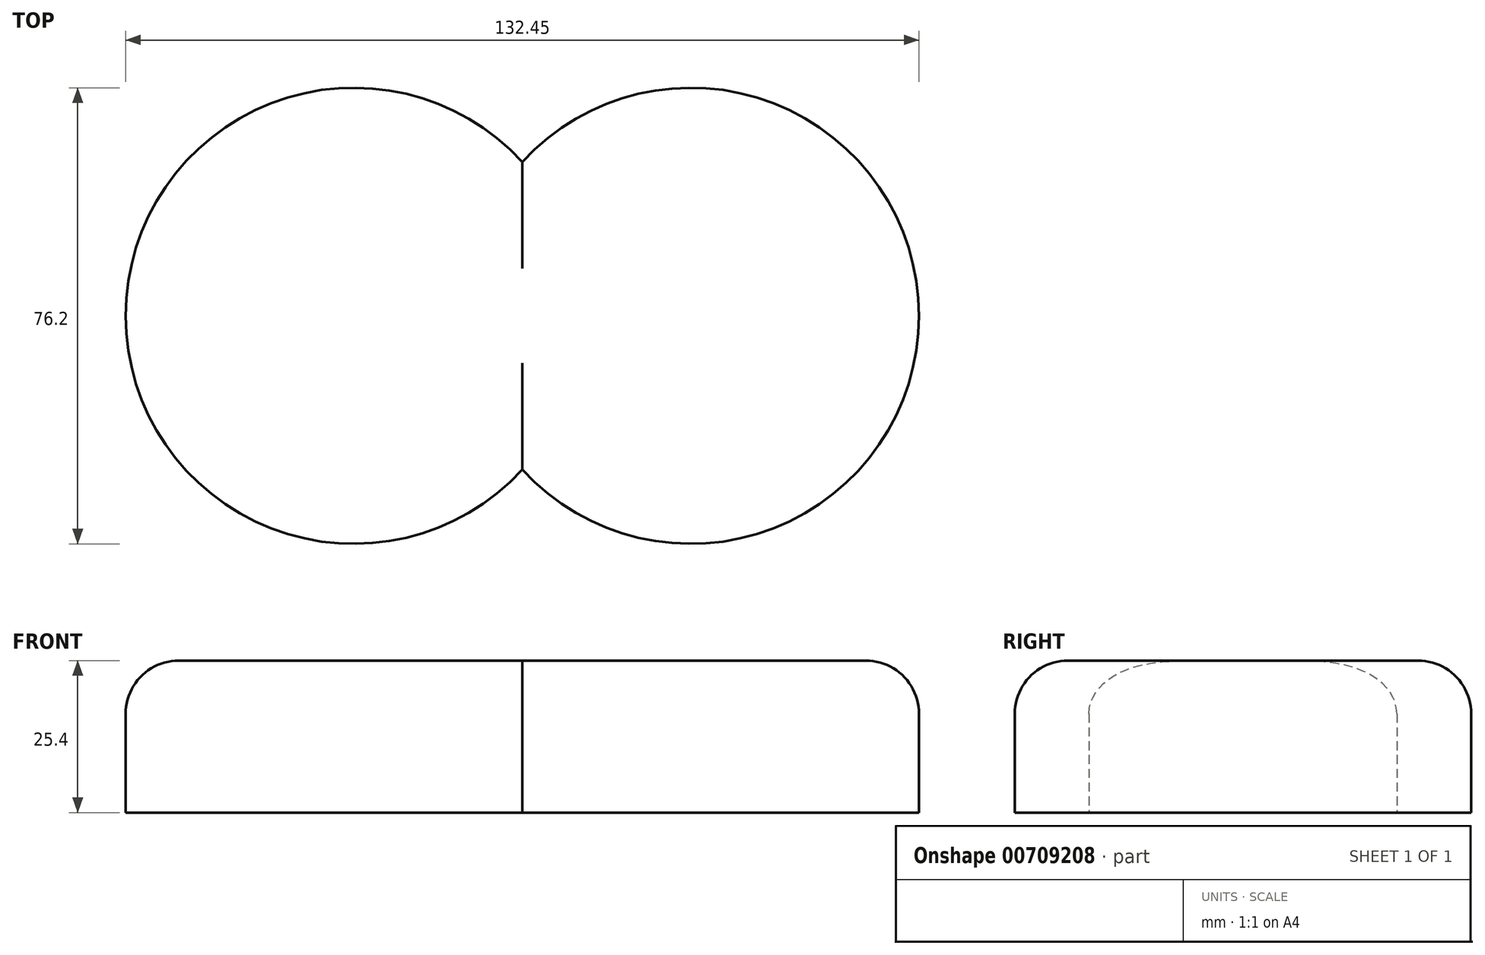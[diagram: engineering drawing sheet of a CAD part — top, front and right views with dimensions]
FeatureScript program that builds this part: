
annotation { "Feature Type Name" : "Feature", "Feature Type Description" : "" }
export const myFeature = defineFeature(function(context is Context, id is Id, definition is map)
    precondition{}
    {
        {
            var Q0;
            Q0=qCreatedBy(makeId("Top.planeOp"),FACE);
            var sketch = newSketch(context, id + "F0", { "sketchPlane" : qUnion([Q0])});
            skArc(sketch, "E0", {"start": v(29.2, -25.7) * mm, "mid": v(95.43, 0) * mm, "end": v(29.2, 25.7) * mm});
            skArc(sketch, "E1", {"start": v(29.2, 25.7) * mm, "mid": v(-37.02, 0) * mm, "end": v(29.2, -25.7) * mm});
            skSolve(sketch);
        }
        {
            var Q0;
            Q0=makeQuery(id+"F0.imprint","IMPRINT",FACE,{"disambiguationData":[TD([[makeQuery(id+"F0.imprint","IMPRINT",EDGE,{"derivedFrom":sQuery(id+"F0.wireOp",EDGE,"E0")}),1.0]])]});
            extrude(context, id + "F1", {"entities" : qUnion([Q0]), "depth" : 25.4 * mm, "offsetDistance" : 25.4 * mm});
        }
        {
            var Q0;
            Q0=makeQuery(id+"F1.opExtrude","CAP_EDGE",EDGE,{"disambiguationData":[OSD([sQuery(id+"F0.wireOp",EDGE,"E0")])],"isStart":false});
            var Q1;
            Q1=makeQuery(id+"F1.opExtrude","CAP_EDGE",EDGE,{"disambiguationData":[OSD([sQuery(id+"F0.wireOp",EDGE,"E1")])],"isStart":false});
            fillet(context, id + "F2", {"entities" : qUnion([Q0, Q1]), "radius" : 8.9 * mm, "tangentPropagation" : true, "allowEdgeOverflow" : false});
        }
    });
